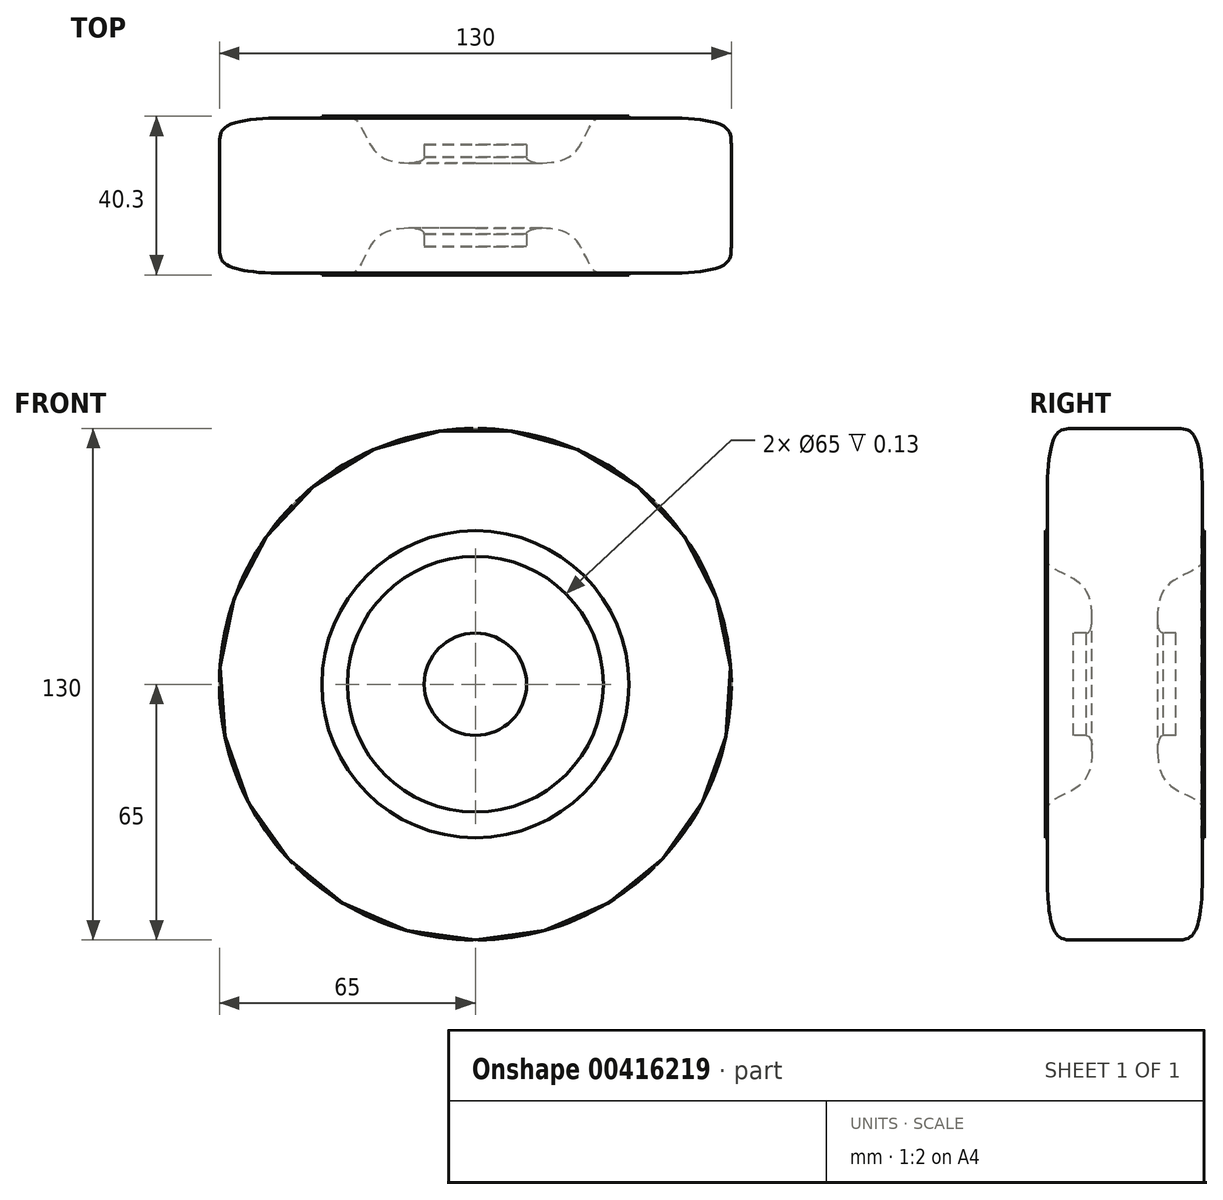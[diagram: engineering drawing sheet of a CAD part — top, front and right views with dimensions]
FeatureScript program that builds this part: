
annotation { "Feature Type Name" : "Feature", "Feature Type Description" : "" }
export const myFeature = defineFeature(function(context is Context, id is Id, definition is map)
    precondition{}
    {
        {
            var Q0;
            Q0=qCreatedBy(makeId("Right.planeOp"),FACE);
            var sketch = newSketch(context, id + "F0", { "sketchPlane" : qUnion([Q0])});
            skLineSegment(sketch, "E0", {"start": v(-10, 0) * mm, "end": v(-10, 10) * mm});
            skLineSegment(sketch, "E1", {"start": v(-10, 10) * mm, "end": v(-7.5, 10) * mm});
            skLineSegment(sketch, "E2", {"start": v(0, 50) * mm, "end": v(-10, 50) * mm});
            skPoint(sketch, "E3.endSnap0", {"position": v(0, 25) * mm});
            skFitSpline(sketch, "E4", {"points": [v(-7.5, 10) * mm, v(-6.58, 15.44) * mm, v(-9.3, 20.11) * mm, v(-14.02, 22.7) * mm, v(-15.4, 25) * mm], "startDerivative": vector(13.01, 0.19) * mm, "endDerivative": vector(0.04, 16.96) * mm});
            skLineSegment(sketch, "E5", {"start": v(-15.4, 25) * mm, "end": v(-15.5, 25) * mm});
            skLineSegment(sketch, "E6", {"start": v(-15.5, 25) * mm, "end": v(-15.5, 30) * mm});
            skLineSegment(sketch, "E7", {"start": v(-15.5, 30) * mm, "end": v(-15, 30) * mm});
            skFitSpline(sketch, "E8", {"points": [v(-15, 30) * mm, v(-15, 42.2) * mm, v(-13.54, 48.58) * mm, v(-10, 50) * mm], "startDerivative": vector(-0.58, 28.7) * mm, "endDerivative": vector(25.34, -0.17) * mm});
            skLineSegment(sketch, "E9.MirrorCS", {"start": v(0, 50) * mm, "end": v(10, 50) * mm});
            skFitSpline(sketch, "E10.MirrorCS", {"points": [v(15, 30) * mm, v(15, 42.2) * mm, v(13.54, 48.58) * mm, v(10, 50) * mm], "startDerivative": vector(0.58, 28.7) * mm, "endDerivative": vector(-25.34, -0.17) * mm});
            skLineSegment(sketch, "E11.MirrorCS", {"start": v(15.5, 30) * mm, "end": v(15, 30) * mm});
            skLineSegment(sketch, "E12.MirrorCS", {"start": v(15.5, 25) * mm, "end": v(15.5, 30) * mm});
            skLineSegment(sketch, "E13.MirrorCS", {"start": v(15.4, 25) * mm, "end": v(15.5, 25) * mm});
            skFitSpline(sketch, "E14.MirrorCS", {"points": [v(7.5, 10) * mm, v(6.58, 15.44) * mm, v(9.3, 20.11) * mm, v(14.02, 22.7) * mm, v(15.4, 25) * mm], "startDerivative": vector(-13.01, 0.19) * mm, "endDerivative": vector(-0.04, 16.96) * mm});
            skLineSegment(sketch, "E15.MirrorCS", {"start": v(10, 10) * mm, "end": v(7.5, 10) * mm});
            skLineSegment(sketch, "E16.MirrorCS", {"start": v(10, 0) * mm, "end": v(10, 10) * mm});
            skLineSegment(sketch, "E17", {"start": v(-10, 0) * mm, "end": v(10, 0) * mm});
            skSolve(sketch);
        }
        {
            var Q0;
            Q0=makeQuery(id+"F0.imprint","IMPRINT",FACE,{"disambiguationData":[TD([[makeQuery(id+"F0.imprint","IMPRINT",EDGE,{"derivedFrom":sQuery(id+"F0.wireOp",EDGE,"E0")}),-1.0]])]});
            var Q1;
            Q1=sQuery(id+"F0.wireOp",EDGE,"E17");
            revolve(context, id + "F1", {"entities" : qUnion([Q0]), "axis" : qUnion([Q1]), "revolveType" : RevolveType.FULL});
        }
        {
            var Q0;
            Q0=qCreatedBy(makeId("Right.planeOp"),FACE);
            var sketch = newSketch(context, id + "F2", { "sketchPlane" : qUnion([Q0])});
            skLineSegment(sketch, "E18", {"start": v(7.37, 21.83) * mm, "end": v(2.51, 10.01) * mm});
            skLineSegment(sketch, "E19", {"start": v(2.51, 10.01) * mm, "end": v(0.8, 10.01) * mm});
            skLineSegment(sketch, "E20", {"start": v(0.8, 10.01) * mm, "end": v(0.8, 21.83) * mm});
            skLineSegment(sketch, "E21", {"start": v(0.8, 21.83) * mm, "end": v(7.37, 21.83) * mm});
            skSolve(sketch);
        }
        {
            var Q0;
            Q0 = qSketchRegion(id + "F2", true);
            extrude(context, id + "F3", {"entities" : qUnion([Q0]), "operationType" : NewBodyOperationType.ADD, "endBound" : BoundingType.SYMMETRIC, "oppositeDirection" : true, "depth" : 1 * mm});
        }
        {
            var Q0;
            Q0=makeQuery(id+"F1.opRevolve","SWEPT_BODY",BODY,{"disambiguationData":[OSD([sQuery(id+"F0.wireOp",EDGE,"E0"),sQuery(id+"F0.wireOp",EDGE,"E1"),sQuery(id+"F0.wireOp",EDGE,"E2"),sQuery(id+"F0.wireOp",EDGE,"E4"),sQuery(id+"F0.wireOp",EDGE,"E5"),sQuery(id+"F0.wireOp",EDGE,"E6"),sQuery(id+"F0.wireOp",EDGE,"E7"),sQuery(id+"F0.wireOp",EDGE,"E8"),sQuery(id+"F0.wireOp",EDGE,"33f3707a-de8b-465b-b82e-c2ffef0ab53a0.MirrorCS"),sQuery(id+"F0.wireOp",EDGE,"952255b9-8d48-4b9f-b91a-297c88e465910.MirrorCS"),sQuery(id+"F0.wireOp",EDGE,"99bda9d9-80f6-40b9-8c5f-c10db237e9e80.MirrorCS"),sQuery(id+"F0.wireOp",EDGE,"a012b006-2d33-40b9-9adb-d6a51fecc9200.MirrorCS"),sQuery(id+"F0.wireOp",EDGE,"61dcf5bb-d908-43ed-8fdd-faceb35704030.MirrorCS"),sQuery(id+"F0.wireOp",EDGE,"dc890ebd-95fb-44d0-8c1f-f0bfb2a54b3d0.MirrorCS"),sQuery(id+"F0.wireOp",EDGE,"defd8256-2f04-42be-94dc-b612378d45330.MirrorCS"),sQuery(id+"F0.wireOp",EDGE,"0cb013ff-c976-48c7-95af-affbcfeb90a30.MirrorCS"),sQuery(id+"F0.wireOp",EDGE,"dd7Xzq6w-c3vy-Ekbr-wrdh-kQHtQSuKWDRc")])]});
            var Q1;
            Q1=qCreatedBy(makeId("Origin.pointOp"),VERTEX);
            transform(context, id + "F4", {"entities" : qUnion([Q0]), "transformType" : TransformType.SCALE_UNIFORMLY, "scale" : 1.3, "scalePoint" : qUnion([Q1]), "makeCopy" : false});
        }
    });
